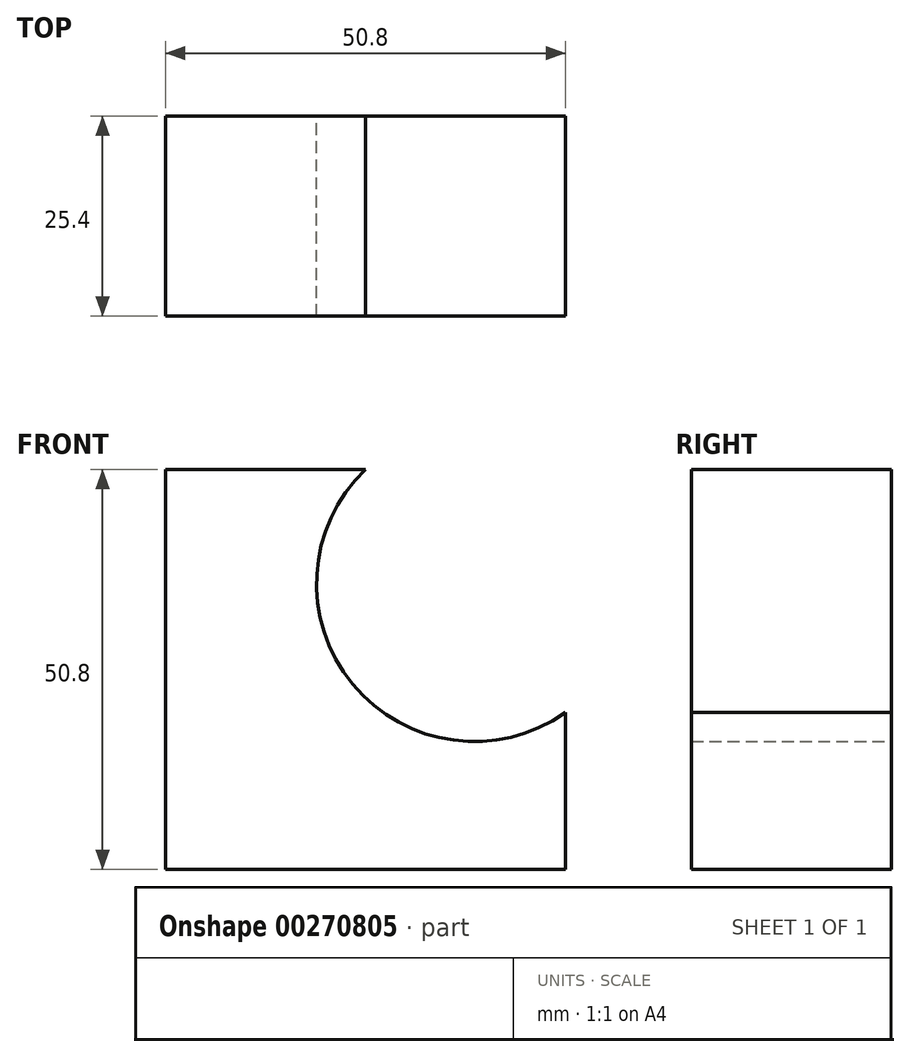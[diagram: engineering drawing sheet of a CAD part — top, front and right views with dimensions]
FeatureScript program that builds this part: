
annotation { "Feature Type Name" : "Feature", "Feature Type Description" : "" }
export const myFeature = defineFeature(function(context is Context, id is Id, definition is map)
    precondition{}
    {
        {
            var Q0;
            Q0=qCreatedBy(makeId("Front.planeOp"),FACE);
            var sketch = newSketch(context, id + "F0", { "sketchPlane" : qUnion([Q0])});
            skLineSegment(sketch, "E0", {"start": v(0, 0) * mm, "end": v(-50.8, 0) * mm});
            skLineSegment(sketch, "E1", {"start": v(-50.8, 0) * mm, "end": v(-50.8, 50.8) * mm});
            skLineSegment(sketch, "E2", {"start": v(-50.8, 50.8) * mm, "end": v(-25.4, 50.8) * mm});
            skArc(sketch, "E3", {"start": v(-25.4, 50.8) * mm, "mid": v(-27.06, 23.55) * mm, "end": v(0, 19.93) * mm});
            skLineSegment(sketch, "E4", {"start": v(0, 19.93) * mm, "end": v(0, 0) * mm});
            skSolve(sketch);
        }
        {
            var Q0;
            Q0 = qSketchRegion(id + "F0", true);
            extrude(context, id + "F1", {"entities" : qUnion([Q0]), "depth" : 25.4 * mm});
        }
    });
